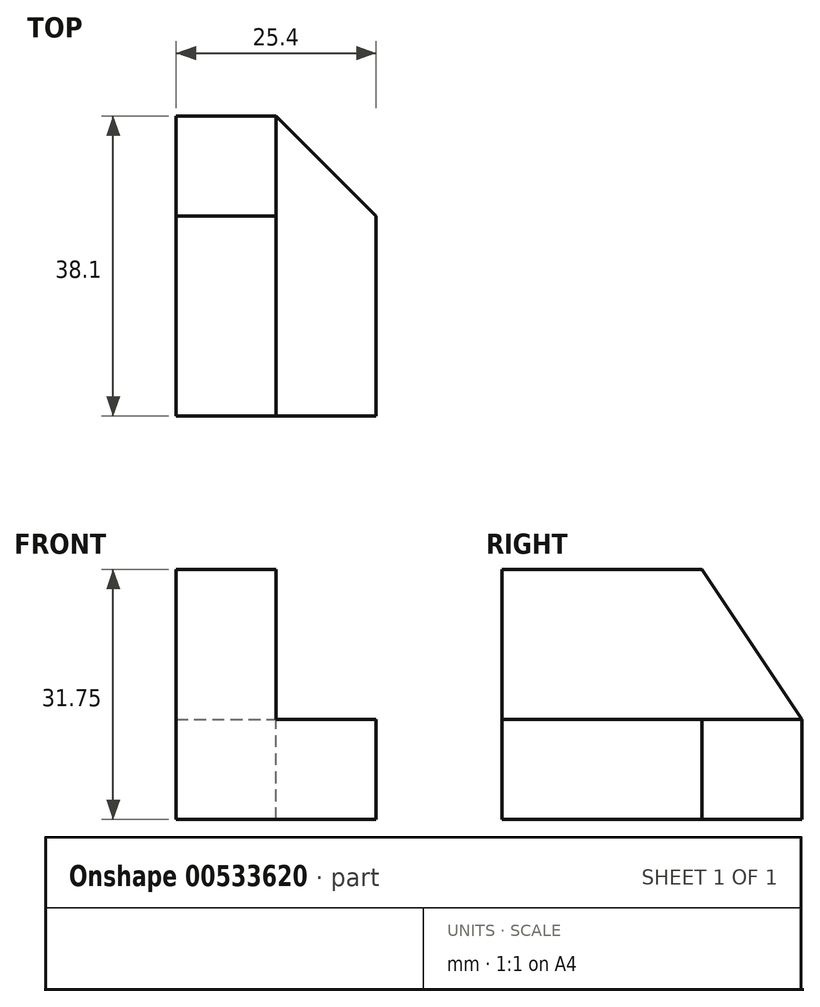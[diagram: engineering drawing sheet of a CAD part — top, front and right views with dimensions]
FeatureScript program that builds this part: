
annotation { "Feature Type Name" : "Feature", "Feature Type Description" : "" }
export const myFeature = defineFeature(function(context is Context, id is Id, definition is map)
    precondition{}
    {
        {
            var Q0;
            Q0=qCreatedBy(makeId("Right.planeOp"),FACE);
            var sketch = newSketch(context, id + "F0", { "sketchPlane" : qUnion([Q0])});
            skLineSegment(sketch, "E0.bottom", {"start": v(52.05, 48) * mm, "end": v(13.95, 48) * mm});
            skLineSegment(sketch, "E0.top", {"start": v(52.05, 16.24) * mm, "end": v(13.95, 16.24) * mm});
            skLineSegment(sketch, "E0.left", {"start": v(52.05, 48) * mm, "end": v(52.05, 16.24) * mm});
            skLineSegment(sketch, "E0.right", {"start": v(13.95, 48) * mm, "end": v(13.95, 16.24) * mm});
            skSolve(sketch);
        }
        {
            var Q0;
            Q0 = qSketchRegion(id + "F0", true);
            extrude(context, id + "F1", {"entities" : qUnion([Q0]), "depth" : 12.7 * mm, "offsetDistance" : 25.4 * mm});
        }
        {
            var Q0;
            Q0=makeQuery(id+"F1.opExtrude","CAP_FACE",FACE,{"disambiguationData":[OSD([sQuery(id+"F0.wireOp",EDGE,"E0.bottom"),sQuery(id+"F0.wireOp",EDGE,"E0.top"),sQuery(id+"F0.wireOp",EDGE,"E0.left"),sQuery(id+"F0.wireOp",EDGE,"E0.right")])],"isStart":false});
            var sketch = newSketch(context, id + "F2", { "sketchPlane" : qUnion([Q0])});
            skLineSegment(sketch, "E1", {"start": v(13.95, 28.94) * mm, "end": v(52.05, 28.94) * mm});
            skLineSegment(sketch, "E2", {"start": v(52.05, 28.94) * mm, "end": v(52.05, 16.24) * mm});
            skLineSegment(sketch, "E3", {"start": v(52.05, 16.24) * mm, "end": v(13.95, 16.24) * mm});
            skLineSegment(sketch, "E4", {"start": v(13.95, 16.24) * mm, "end": v(13.95, 28.94) * mm});
            skSolve(sketch);
        }
        {
            var Q0;
            Q0 = qSketchRegion(id + "F2", true);
            extrude(context, id + "F3", {"entities" : qUnion([Q0]), "operationType" : NewBodyOperationType.ADD, "depth" : 12.7 * mm, "offsetDistance" : 25.4 * mm});
        }
        {
            var Q0;
            Q0=makeQuery(id+"F1.opExtrude","CAP_FACE",FACE,{"disambiguationData":[OSD([sQuery(id+"F0.wireOp",EDGE,"E0.bottom"),sQuery(id+"F0.wireOp",EDGE,"E0.top"),sQuery(id+"F0.wireOp",EDGE,"E0.left"),sQuery(id+"F0.wireOp",EDGE,"E0.right")])],"isStart":false});
            var sketch = newSketch(context, id + "F4", { "sketchPlane" : qUnion([Q0])});
            skLineSegment(sketch, "E5", {"start": v(52.05, 28.94) * mm, "end": v(39.35, 48) * mm});
            skSolve(sketch);
        }
        {
            var Q0;
            Q0 = qSketchRegion(id + "F4", true);
            var Q1;
            {var subQ0=sQuery(id+"F4.wireOp",EDGE,"E5");Q1=makeQuery(id+"F4.imprint","IMPRINT",FACE,{"disambiguationData":[TD([[makeQuery(id+"F4.imprint","IMPRINT",EDGE,{"derivedFrom":subQ0}),-1.0]])]});}
            extrude(context, id + "F5", {"entities" : qUnion([Q0, Q1]), "operationType" : NewBodyOperationType.REMOVE, "oppositeDirection" : true, "depth" : 25.4 * mm, "offsetDistance" : 25.4 * mm});
        }
        {
            var Q0;
            Q0=makeQuery(id+"F3.opExtrude","SWEPT_FACE",FACE,{"disambiguationData":[OSD([sQuery(id+"F2.wireOp",EDGE,"E1")])]});
            var sketch = newSketch(context, id + "F6", { "sketchPlane" : qUnion([Q0])});
            skLineSegment(sketch, "E6", {"start": v(12.7, 52.05) * mm, "end": v(25.4, 39.35) * mm});
            skSolve(sketch);
        }
        {
            var Q0;
            {var subQ0=sQuery(id+"F6.wireOp",EDGE,"E6");Q0=makeQuery(id+"F6.imprint","IMPRINT",FACE,{"disambiguationData":[TD([[makeQuery(id+"F6.imprint","IMPRINT",EDGE,{"derivedFrom":subQ0}),1.0]])]});}
            extrude(context, id + "F7", {"entities" : qUnion([Q0]), "operationType" : NewBodyOperationType.REMOVE, "oppositeDirection" : true, "depth" : 25.4 * mm, "offsetDistance" : 25.4 * mm});
        }
    });
